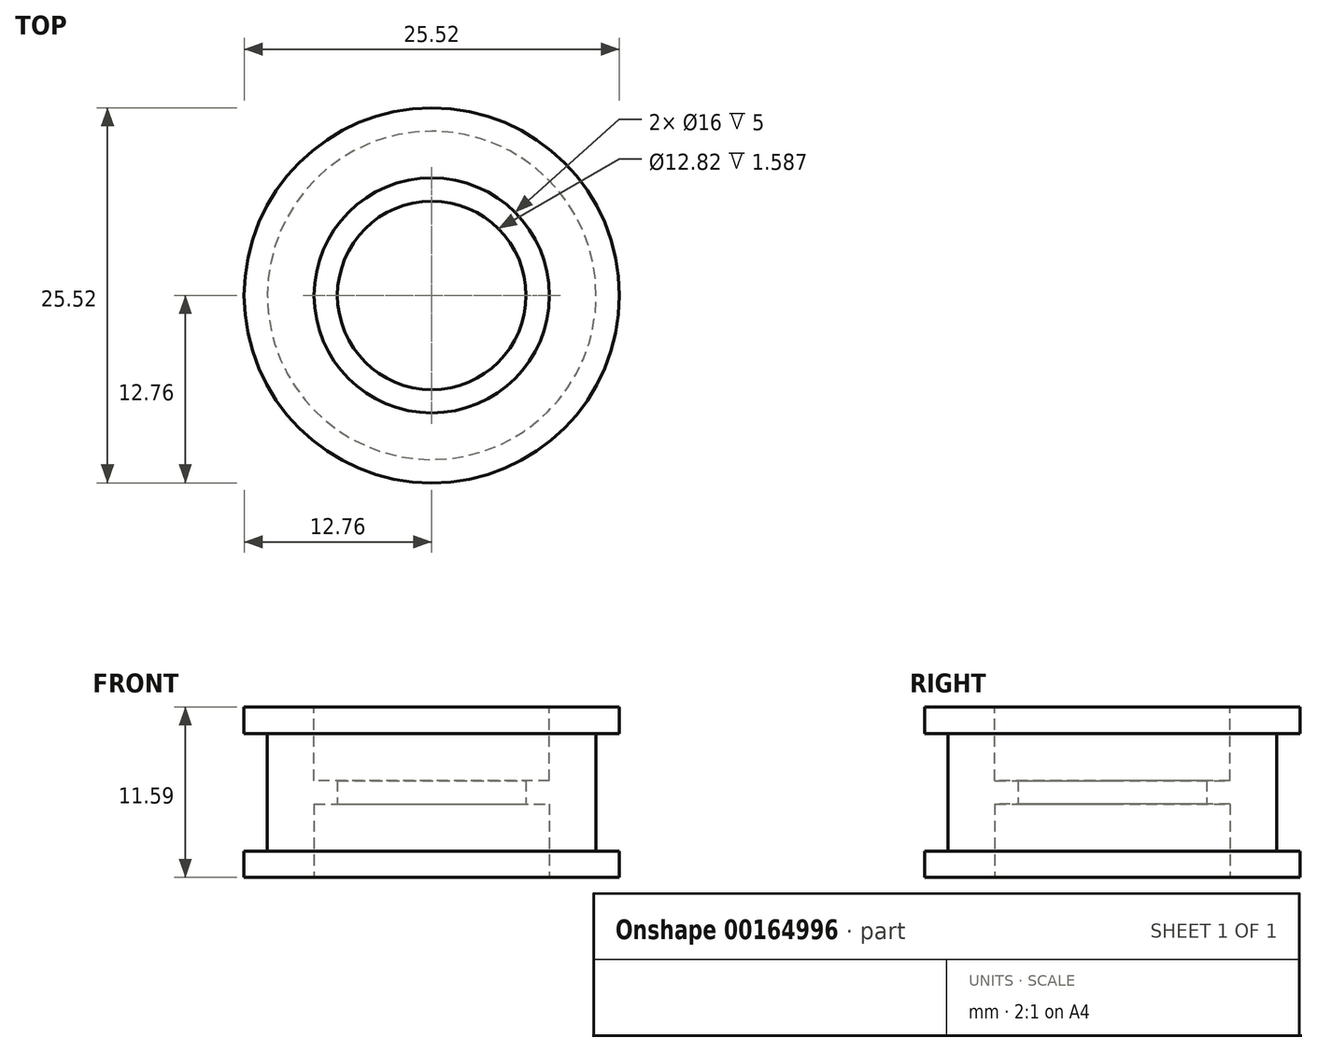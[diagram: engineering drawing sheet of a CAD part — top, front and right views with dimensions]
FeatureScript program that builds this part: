
annotation { "Feature Type Name" : "Feature", "Feature Type Description" : "" }
export const myFeature = defineFeature(function(context is Context, id is Id, definition is map)
    precondition{}
    {
        {
            var Q0;
            Q0=qCreatedBy(makeId("Top.planeOp"),FACE);
            var sketch = newSketch(context, id + "F0", { "sketchPlane" : qUnion([Q0])});
            skCircle(sketch, "E0", {"center": v(0, 0) * mm, "radius": 8 * mm, "construction": true});
            skCircle(sketch, "E1", {"center": v(0, 0) * mm, "radius": 6.41 * mm});
            skCircle(sketch, "E2", {"center": v(0, 0) * mm, "radius": 12.76 * mm});
            skSolve(sketch);
        }
        {
            var Q0;
            Q0 = qSketchRegion(id + "F0", true);
            extrude(context, id + "F1", {"entities" : qUnion([Q0]), "depth" : 1.8 * mm});
        }
        {
            var Q0;
            Q0=makeQuery(id+"F1.opExtrude","CAP_FACE",FACE,{"disambiguationData":[OSD([sQuery(id+"F0.wireOp",EDGE,"E1"),sQuery(id+"F0.wireOp",EDGE,"E2")])],"isStart":false});
            var sketch = newSketch(context, id + "F2", { "sketchPlane" : qUnion([Q0])});
            skCircle(sketch, "E3", {"center": v(0, 0) * mm, "radius": 6.41 * mm});
            skCircle(sketch, "E4", {"center": v(0, 0) * mm, "radius": 11.17 * mm});
            skSolve(sketch);
        }
        {
            var Q0;
            Q0 = qSketchRegion(id + "F2", true);
            extrude(context, id + "F3", {"entities" : qUnion([Q0]), "operationType" : NewBodyOperationType.ADD, "depth" : 8 * mm});
        }
        {
            var Q0;
            Q0=makeQuery(id+"F3.opExtrude","CAP_FACE",FACE,{"disambiguationData":[OSD([sQuery(id+"F2.wireOp",EDGE,"E3"),sQuery(id+"F2.wireOp",EDGE,"E4")])],"isStart":false});
            var sketch = newSketch(context, id + "F4", { "sketchPlane" : qUnion([Q0])});
            skCircle(sketch, "E5", {"center": v(0, 0) * mm, "radius": 6.41 * mm});
            skCircle(sketch, "E6", {"center": v(0, 0) * mm, "radius": 12.76 * mm});
            skSolve(sketch);
        }
        {
            var Q0;
            Q0 = qSketchRegion(id + "F4", true);
            extrude(context, id + "F5", {"entities" : qUnion([Q0]), "operationType" : NewBodyOperationType.ADD, "depth" : 1.8 * mm});
        }
        {
            var Q0;
            Q0=makeQuery(id+"F5.opExtrude","CAP_FACE",FACE,{"disambiguationData":[OSD([sQuery(id+"F4.wireOp",EDGE,"E5"),sQuery(id+"F4.wireOp",EDGE,"E6")])],"isStart":false});
            var sketch = newSketch(context, id + "F6", { "sketchPlane" : qUnion([Q0])});
            skCircle(sketch, "E7", {"center": v(0, 0) * mm, "radius": 8 * mm});
            skSolve(sketch);
        }
        {
            var Q0;
            Q0 = qSketchRegion(id + "F6", true);
            extrude(context, id + "F7", {"entities" : qUnion([Q0]), "operationType" : NewBodyOperationType.REMOVE, "oppositeDirection" : true, "depth" : 5 * mm});
        }
        {
            var Q0;
            Q0=makeQuery(id+"F1.opExtrude","CAP_FACE",FACE,{"disambiguationData":[OSD([sQuery(id+"F0.wireOp",EDGE,"E1"),sQuery(id+"F0.wireOp",EDGE,"E2")])],"isStart":true});
            var sketch = newSketch(context, id + "F8", { "sketchPlane" : qUnion([Q0])});
            skCircle(sketch, "E8", {"center": v(0, 0) * mm, "radius": 8 * mm});
            skSolve(sketch);
        }
        {
            var Q0;
            Q0 = qSketchRegion(id + "F8", true);
            extrude(context, id + "F9", {"entities" : qUnion([Q0]), "operationType" : NewBodyOperationType.REMOVE, "oppositeDirection" : true, "depth" : 5 * mm});
        }
    });
